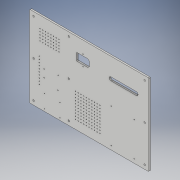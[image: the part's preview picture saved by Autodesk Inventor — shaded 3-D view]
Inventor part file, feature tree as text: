
AUTODESK INVENTOR PART (.ipt)
format: ipt  version: 2019 (Build 230136000, 136)  size: 451,584 bytes
history: native  units: mm
features: reference x24, extrude x10, sketch x10, other x9, projected_geometry x1, helix x1
ambient origin geometry x8: Origin, YZ Plane, XZ Plane, XY Plane, X Axis, Y Axis, Z Axis, Center Point
bodies: Solid1 (feature_tree)
feature tree (55):
  extrude  "Extrusion1"  Depth=2.0mm
  extrude  "Extrusion2"  Depth=6.0mm
  extrude  "Extrusion3"  Depth=6.0mm
  extrude  "Extrusion4"  Depth=10.0mm TaperAngle=0.0deg
  extrude  "Extrusion5"  Depth=6.0mm
  extrude  "Extrusion6"  Depth=6.0mm
  extrude  "Extrusion7"  Depth=6.0mm TaperAngle=0.0deg
  extrude  "Extrusion8"  Depth=6.0mm TaperAngle=0.0deg
  extrude  "Extrusion9"  Depth=6.0mm TaperAngle=0.0deg
  extrude  "Extrusion10"  Depth=10.0mm
  sketch  "Sketch1"  dims[d0=300.0mm d1=2.0mm]
  reference  "Reference1"
  reference  "Reference2"
  reference  "Reference3"
  sketch  "Sketch2"  dims[d2=6.0mm d3=0.0mm d4=6.0mm]
  reference  "Reference4"
  reference  "Reference5"
  reference  "Reference6"
  sketch  "Sketch3"  dims[d5=6.0mm d6=6.0mm]
  reference  "Reference7"
  reference  "Reference8"
  sketch  "Sketch4"  dims[d7=6.0mm d8=10.0mm d9=0.0mm]
  reference  "Reference9"
  reference  "Reference10"
  reference  "Reference11"
  reference  "Reference12"
  reference  "Reference13"
  reference  "Reference14"
  reference  "Reference15"
  reference  "Reference16"
  reference  "Reference17"
  reference  "Reference18"
  sketch  "Sketch5"  dims[d10=2.0mm d11=6.0mm]
  projected_geometry  "Projected Loop1"
  sketch  "Sketch6"  dims[d12=6.0mm d13=6.0mm]
  reference  "Reference19"
  reference  "Reference20"
  reference  "Reference21"
  reference  "Reference22"
  sketch  "Sketch7"  dims[d14=6.0mm d15=0.0mm d16=6.0mm d17=0.0mm]
  sketch  "Sketch8"  dims[d18=0.2mm d19=6.0mm d20=0.0mm]
  sketch  "Sketch9"  dims[d21=6.0mm d22=0.0mm d23=6.0mm d24=0.0mm]
  sketch  "Sketch10"  dims[d25=3.0mm d26=100.0mm d28=10.0mm d29=100.0mm d31=10.0mm d34=3.0mm d35=100.0mm d37=10.0mm d38=10.0mm d40=10.0mm d42=6.0mm d43=0.0mm d44=3.0mm d45=80.0mm d47=10.0mm d48=50.0mm d50=10.0mm d53=6.0mm d54=0.0mm d55=6.0mm d56=0.0mm]
  reference  "Reference23"
  reference  "Reference24"
  other  "<userpath>\Documents\CAD Files\Helix DLP\Helix DLP.iam"
  helix  "Helix DLP.iam"  [1 undecoded]
  other  "30X30 - T-slot - Aluminium Profile:1"
  other  "30X30 - T-slot - Aluminium Profile:3"
  other  "30X30 - T-slot - Aluminium Profile_CPY:3"
  other  "30X30 - T-slot - Aluminium Profile:2"
  other  "Raspberry Pi 3 Model B+ Reference Model:1"
  other  "ArduinoUno:1"
  other  "V8_AC switch_1:1"
  other  "24v Smps:1"
note: 1 required parameter value undecoded (feature->parameter linkage not recoverable at this tier; creation-order binding heuristic only, values carry confidence <= 0.55)
